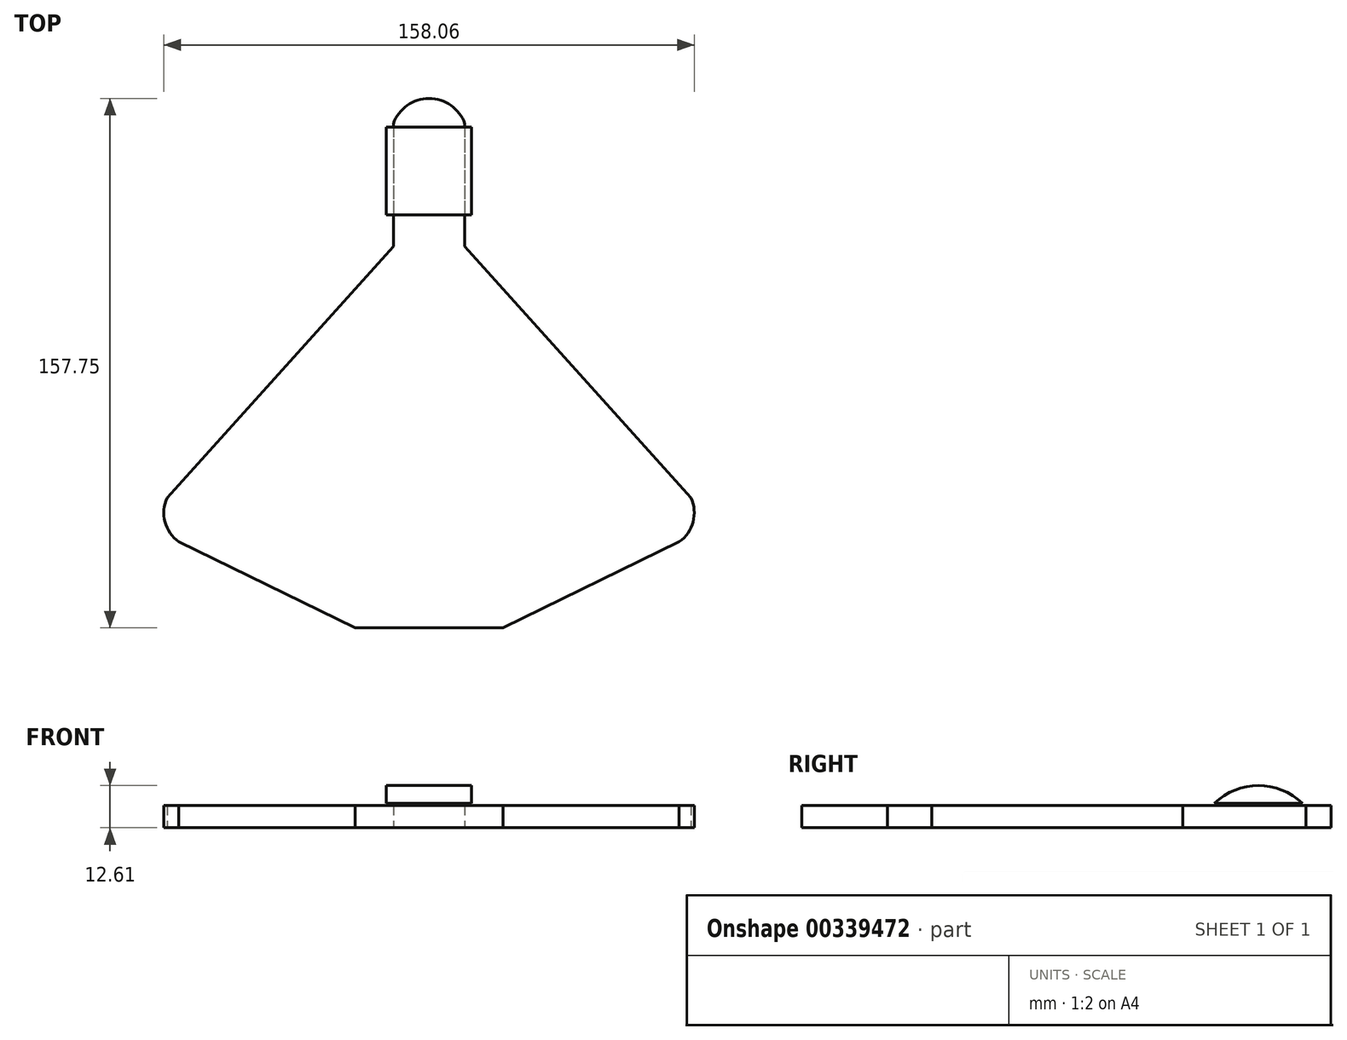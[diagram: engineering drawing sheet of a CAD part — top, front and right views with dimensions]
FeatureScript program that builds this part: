
annotation { "Feature Type Name" : "Feature", "Feature Type Description" : "" }
export const myFeature = defineFeature(function(context is Context, id is Id, definition is map)
    precondition{}
    {
        {
            var Q0;
            Q0=qCreatedBy(makeId("Top.planeOp"),FACE);
            var sketch = newSketch(context, id + "F0", { "sketchPlane" : qUnion([Q0])});
            skLineSegment(sketch, "E0", {"start": v(-10.64, 52.65) * mm, "end": v(-10.64, 14.55) * mm});
            skLineSegment(sketch, "E1", {"start": v(-10.64, 14.55) * mm, "end": v(-78.63, -60.95) * mm});
            skArc(sketch, "E2", {"start": v(-73.89, -55.69) * mm, "mid": v(-78.95, -66.13) * mm, "end": v(-71.45, -74.98) * mm});
            skPoint(sketch, "E2.first.point", {"position": v(-73.89, -55.69) * mm});
            skPoint(sketch, "E2.second.point", {"position": v(-61.6, -72.97) * mm});
            skPoint(sketch, "E2.third.point", {"position": v(-78.63, -67.7) * mm});
            skLineSegment(sketch, "E3", {"start": v(-74.54, -73.48) * mm, "end": v(-22.03, -99.07) * mm});
            skLineSegment(sketch, "E4", {"start": v(-22.03, -99.07) * mm, "end": v(0, -99.07) * mm});
            skLineSegment(sketch, "E5.MirrorCS", {"start": v(10.64, 51.18) * mm, "end": v(10.64, 14.55) * mm});
            skLineSegment(sketch, "E6.MirrorCS", {"start": v(10.64, 14.55) * mm, "end": v(78.63, -60.95) * mm});
            skArc(sketch, "E7.MirrorCS", {"start": v(73.89, -55.69) * mm, "mid": v(78.95, -66.13) * mm, "end": v(71.45, -74.98) * mm});
            skLineSegment(sketch, "E8.MirrorCS", {"start": v(74.54, -73.48) * mm, "end": v(22.03, -99.07) * mm});
            skLineSegment(sketch, "E9.MirrorCS", {"start": v(22.03, -99.07) * mm, "end": v(0, -99.07) * mm});
            skArc(sketch, "E10", {"start": v(10.64, 51.18) * mm, "mid": v(0, 58.68) * mm, "end": v(-10.64, 51.18) * mm});
            skPoint(sketch, "E11.orphan", {"position": v(0, 63.56) * mm});
            skPoint(sketch, "E12.MirrorCS.end.orphan", {"position": v(10.64, 52.65) * mm});
            skSolve(sketch);
        }
        {
            var Q0;
            {var subQ4=sQuery(id+"F0.wireOp",EDGE,"E4");Q0=makeQuery(id+"F0.imprint","IMPRINT",FACE,{"disambiguationData":[TD([[makeQuery(id+"F0.imprint","IMPRINT",EDGE,{"derivedFrom":subQ4}),1.0]])]});}
            extrude(context, id + "F1", {"entities" : qUnion([Q0]), "depth" : 6.7 * mm});
        }
        {
            var Q0;
            Q0=qCreatedBy(makeId("Right.planeOp"),FACE);
            var sketch = newSketch(context, id + "F2", { "sketchPlane" : qUnion([Q0])});
            skArc(sketch, "E13", {"start": v(50.14, 7.26) * mm, "mid": v(37.06, 12.6) * mm, "end": v(23.98, 7.26) * mm});
            skPoint(sketch, "E13.first.point", {"position": v(23.98, 7.26) * mm});
            skPoint(sketch, "E13.second.point", {"position": v(50.14, 7.26) * mm});
            skPoint(sketch, "E13.third.point", {"position": v(39.04, -24.65) * mm});
            skLineSegment(sketch, "E14", {"start": v(23.98, 7.26) * mm, "end": v(50.14, 7.26) * mm});
            skSolve(sketch);
        }
        {
            var Q0;
            Q0=makeQuery(id+"F2.imprint","IMPRINT",FACE,{"disambiguationData":[TD([[makeQuery(id+"F2.imprint","IMPRINT",EDGE,{"derivedFrom":sQuery(id+"F2.wireOp",EDGE,"E13")}),1.0]])]});
            extrude(context, id + "F3", {"entities" : qUnion([Q0]), "endBound" : BoundingType.SYMMETRIC, "depth" : 25.4 * mm});
        }
    });
